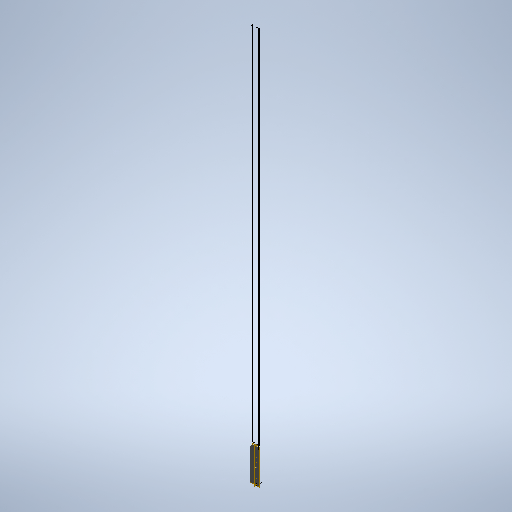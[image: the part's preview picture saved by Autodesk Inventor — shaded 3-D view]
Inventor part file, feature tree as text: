
AUTODESK INVENTOR PART (.ipt)
format: ipt  version: 2025.2 (Build 292293000, 293)  size: 331,776 bytes
history: native  units: mm
features: other x4, extrude x2, sketch x2, pattern_linear x1
ambient origin geometry x8: Origin, YZ Plane, XZ Plane, XY Plane, X Axis, Y Axis, Z Axis, Center Point
bodies: Solid1 (feature_tree)
feature tree (9):
  other  "Annotations"
  extrude  "Extrusion1"  Depth=160.0mm TaperAngle=0.0deg
  extrude  "Extrusion2"  Depth=7.5mm
  pattern_linear  "Rectangular Pattern1"  [2 undecoded]
  sketch  "Sketch_2"  dims[d0=160.0mm d1=0.0mm d2=2.0mm d3=0.0mm]
  sketch  "Sketch_6"  dims[d4=800.0mm d6=22.9mm d7=10.0mm d9=0.0mm d10=2000.0mm d11=7.5mm d12=35.0mm]
  other  "Linear Dimension 1"
  other  "Linear Dimension 2"
  other  "Linear Dimension 3"
note: 2 required parameter values undecoded (feature->parameter linkage not recoverable at this tier; creation-order binding heuristic only, values carry confidence <= 0.55)
